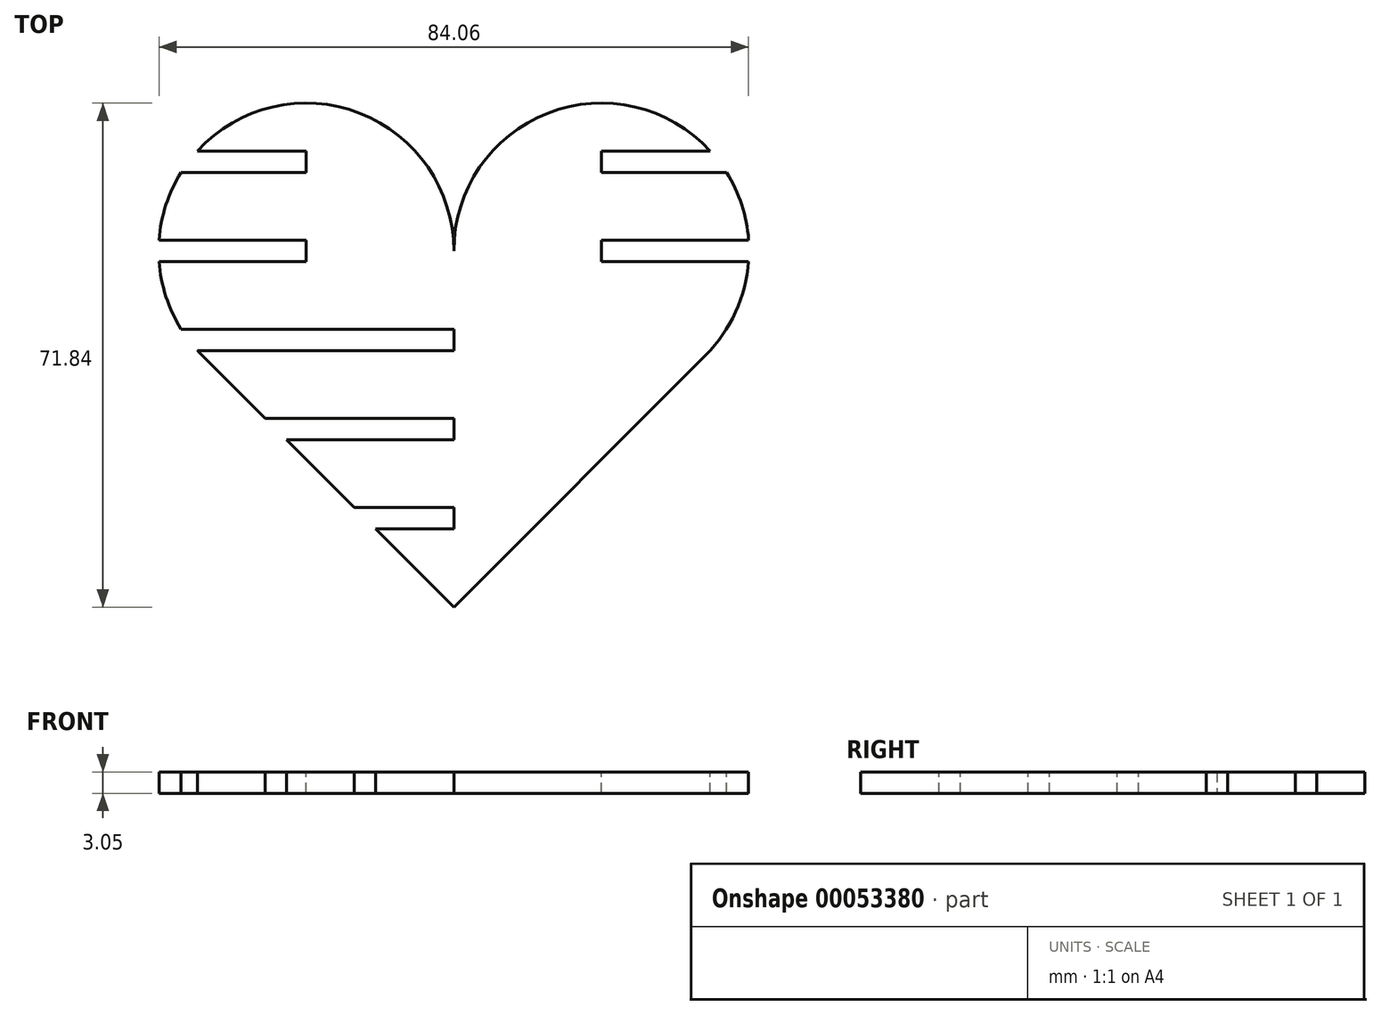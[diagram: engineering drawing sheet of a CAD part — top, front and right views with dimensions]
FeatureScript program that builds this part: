
annotation { "Feature Type Name" : "Feature", "Feature Type Description" : "" }
export const myFeature = defineFeature(function(context is Context, id is Id, definition is map)
    precondition{}
    {
        {
            var Q0;
            Q0=qCreatedBy(makeId("Top.planeOp"),FACE);
            var sketch = newSketch(context, id + "F0", { "sketchPlane" : qUnion([Q0])});
            skLineSegment(sketch, "E0", {"start": v(-50.8, 0) * mm, "end": v(0, -50.8) * mm});
            skLineSegment(sketch, "E1", {"start": v(0, -50.8) * mm, "end": v(50.8, 0) * mm});
            skLineSegment(sketch, "E2", {"start": v(-50.8, 0) * mm, "end": v(50.8, 0) * mm, "construction": true});
            skCircle(sketch, "E3", {"center": v(-21.04, 0) * mm, "radius": 21.04 * mm});
            skCircle(sketch, "E4", {"center": v(21.04, 0) * mm, "radius": 21.04 * mm});
            skSolve(sketch);
        }
        {
            var Q0;
            {var subQ0=sQuery(id+"F0.wireOp",EDGE,"E3");var subQ1=makeQuery(id+"F0.imprint","INTERSECT",VERTEX,{"derivedFrom":[sQuery(id+"F0.wireOp",EDGE,"E0"),subQ0]});Q0=makeQuery(id+"F0.imprint","IMPRINT",FACE,{"disambiguationData":[TD([[makeQuery(id+"F0.imprint","IMPRINT",EDGE,{"disambiguationData":[TD([[subQ1,1.0]])],"derivedFrom":subQ0}),1.0]])]});}
            var Q1;
            {var subQ0=sQuery(id+"F0.wireOp",EDGE,"E4");var subQ1=makeQuery(id+"F0.imprint","INTERSECT",VERTEX,{"derivedFrom":[sQuery(id+"F0.wireOp",EDGE,"E1"),subQ0]});Q1=makeQuery(id+"F0.imprint","IMPRINT",FACE,{"disambiguationData":[TD([[makeQuery(id+"F0.imprint","IMPRINT",EDGE,{"disambiguationData":[TD([[subQ1,1.0]])],"derivedFrom":subQ0}),1.0]])]});}
            var Q2;
            {var subQ0=sQuery(id+"F0.wireOp",EDGE,"E1");var subQ1=sQuery(id+"F0.wireOp",EDGE,"E0");var subQ2=makeQuery(id+"F0.imprint","INTERSECT",VERTEX,{"derivedFrom":[subQ1,subQ0]});Q2=makeQuery(id+"F0.imprint","IMPRINT",FACE,{"disambiguationData":[TD([[makeQuery(id+"F0.imprint","IMPRINT",EDGE,{"disambiguationData":[TD([[subQ2,1.0]])],"derivedFrom":subQ1}),1.0]])]});}
            extrude(context, id + "F1", {"entities" : qUnion([Q0, Q1, Q2]), "depth" : 3.05 * mm});
        }
        {
            var Q0;
            Q0=makeQuery(id+"F1.opExtrude","CAP_FACE",FACE,{"disambiguationData":[OSD([sQuery(id+"F0.wireOp",EDGE,"E0"),sQuery(id+"F0.wireOp",EDGE,"E1"),sQuery(id+"F0.wireOp",EDGE,"E3"),sQuery(id+"F0.wireOp",EDGE,"E4")])],"isStart":false});
            var sketch = newSketch(context, id + "F2", { "sketchPlane" : qUnion([Q0])});
            skCircle(sketch, "E5", {"center": v(-21.04, 0) * mm, "radius": 21.04 * mm, "construction": true});
            skCircle(sketch, "E6", {"center": v(21.04, 0) * mm, "radius": 21.04 * mm, "construction": true});
            skLineSegment(sketch, "E7.bottom", {"start": v(-42.08, -1.52) * mm, "end": v(-21.04, -1.52) * mm});
            skLineSegment(sketch, "E7.top", {"start": v(-42.08, 1.52) * mm, "end": v(-21.04, 1.52) * mm});
            skLineSegment(sketch, "E7.left", {"start": v(-42.08, -1.52) * mm, "end": v(-42.08, 1.52) * mm});
            skLineSegment(sketch, "E7.right", {"start": v(-21.04, -1.52) * mm, "end": v(-21.04, 1.52) * mm});
            skLineSegment(sketch, "E8.bottom", {"start": v(21.04, -1.52) * mm, "end": v(42.08, -1.52) * mm});
            skLineSegment(sketch, "E8.top", {"start": v(21.04, 1.52) * mm, "end": v(42.08, 1.52) * mm});
            skLineSegment(sketch, "E8.left", {"start": v(21.04, -1.52) * mm, "end": v(21.04, 1.52) * mm});
            skLineSegment(sketch, "E8.right", {"start": v(42.08, -1.52) * mm, "end": v(42.08, 1.52) * mm});
            skPoint(sketch, "E9", {"position": v(-42.08, 0) * mm});
            skPoint(sketch, "E10", {"position": v(42.08, 0) * mm});
            skLineSegment(sketch, "E11", {"start": v(0, -50.8) * mm, "end": v(0, -25.4) * mm, "construction": true});
            skLineSegment(sketch, "E12", {"start": v(0, -25.4) * mm, "end": v(0, 0) * mm, "construction": true});
            skPoint(sketch, "E13", {"position": v(0, -12.7) * mm});
            skPoint(sketch, "E14", {"position": v(0, -38.1) * mm});
            skLineSegment(sketch, "E15.bottom", {"start": v(-38.87, -14.22) * mm, "end": v(0, -14.22) * mm});
            skLineSegment(sketch, "E15.top", {"start": v(-38.87, -11.18) * mm, "end": v(0, -11.18) * mm});
            skLineSegment(sketch, "E15.left", {"start": v(-38.87, -14.22) * mm, "end": v(-38.87, -11.18) * mm});
            skLineSegment(sketch, "E15.right", {"start": v(0, -14.22) * mm, "end": v(0, -11.18) * mm});
            skLineSegment(sketch, "E16.bottom", {"start": v(-26.92, -26.92) * mm, "end": v(0, -26.92) * mm});
            skLineSegment(sketch, "E16.top", {"start": v(-26.92, -23.88) * mm, "end": v(0, -23.88) * mm});
            skLineSegment(sketch, "E16.left", {"start": v(-26.92, -26.92) * mm, "end": v(-26.92, -23.88) * mm});
            skLineSegment(sketch, "E16.right", {"start": v(0, -26.92) * mm, "end": v(0, -23.88) * mm});
            skLineSegment(sketch, "E17.bottom", {"start": v(-14.22, -39.62) * mm, "end": v(0, -39.62) * mm});
            skLineSegment(sketch, "E17.top", {"start": v(-14.22, -36.58) * mm, "end": v(0, -36.58) * mm});
            skLineSegment(sketch, "E17.left", {"start": v(-14.22, -39.62) * mm, "end": v(-14.22, -36.58) * mm});
            skLineSegment(sketch, "E17.right", {"start": v(0, -39.62) * mm, "end": v(0, -36.58) * mm});
            skLineSegment(sketch, "E18.bottom", {"start": v(-38.87, 11.18) * mm, "end": v(-21.04, 11.18) * mm});
            skLineSegment(sketch, "E18.top", {"start": v(-38.87, 14.22) * mm, "end": v(-21.04, 14.22) * mm});
            skLineSegment(sketch, "E18.left", {"start": v(-38.87, 14.22) * mm, "end": v(-38.87, 11.18) * mm});
            skLineSegment(sketch, "E18.right", {"start": v(-21.04, 14.22) * mm, "end": v(-21.04, 11.18) * mm});
            skCircle(sketch, "E19", {"center": v(0, 0) * mm, "radius": 12.7 * mm, "construction": true});
            skPoint(sketch, "E20", {"position": v(-38.87, -12.7) * mm});
            skPoint(sketch, "E21", {"position": v(-26.92, -25.4) * mm});
            skPoint(sketch, "E22", {"position": v(-14.22, -38.1) * mm});
            skPoint(sketch, "E23", {"position": v(-38.87, 12.7) * mm});
            skLineSegment(sketch, "E24", {"start": v(-21.04, 12.7) * mm, "end": v(21.04, 12.7) * mm, "construction": true});
            skLineSegment(sketch, "E25.bottom", {"start": v(21.04, 14.22) * mm, "end": v(38.87, 14.22) * mm});
            skLineSegment(sketch, "E25.top", {"start": v(21.04, 11.18) * mm, "end": v(38.87, 11.18) * mm});
            skLineSegment(sketch, "E25.left", {"start": v(21.04, 14.22) * mm, "end": v(21.04, 11.18) * mm});
            skLineSegment(sketch, "E25.right", {"start": v(38.87, 14.22) * mm, "end": v(38.87, 11.18) * mm});
            skPoint(sketch, "E26", {"position": v(38.87, 12.7) * mm});
            skSolve(sketch);
        }
        {
            var Q0;
            {var subQ0=sQuery(id+"F2.wireOp",EDGE,"E18.bottom");Q0=makeQuery(id+"F2.imprint","IMPRINT",FACE,{"disambiguationData":[TD([[makeQuery(id+"F2.imprint","IMPRINT",EDGE,{"derivedFrom":subQ0}),1.0]])]});}
            var Q1;
            {var subQ4=sQuery(id+"F2.wireOp",EDGE,"E25.top");Q1=makeQuery(id+"F2.imprint","IMPRINT",FACE,{"disambiguationData":[TD([[makeQuery(id+"F2.imprint","IMPRINT",EDGE,{"derivedFrom":subQ4}),1.0]])]});}
            var Q2;
            {var subQ0=sQuery(id+"F2.wireOp",EDGE,"E8.left");Q2=makeQuery(id+"F2.imprint","IMPRINT",FACE,{"disambiguationData":[TD([[makeQuery(id+"F2.imprint","IMPRINT",EDGE,{"derivedFrom":subQ0}),-1.0]])]});}
            var Q3;
            {var subQ4=sQuery(id+"F2.wireOp",EDGE,"E7.right");Q3=makeQuery(id+"F2.imprint","IMPRINT",FACE,{"disambiguationData":[TD([[makeQuery(id+"F2.imprint","IMPRINT",EDGE,{"derivedFrom":subQ4}),1.0]])]});}
            var Q4;
            {var subQ0=sQuery(id+"F2.wireOp",EDGE,"E15.right");Q4=makeQuery(id+"F2.imprint","IMPRINT",FACE,{"disambiguationData":[TD([[makeQuery(id+"F2.imprint","IMPRINT",EDGE,{"derivedFrom":subQ0}),1.0]])]});}
            var Q5;
            {var subQ4=sQuery(id+"F2.wireOp",EDGE,"E16.top");Q5=makeQuery(id+"F2.imprint","IMPRINT",FACE,{"disambiguationData":[TD([[makeQuery(id+"F2.imprint","IMPRINT",EDGE,{"derivedFrom":subQ4}),-1.0]])]});}
            var Q6;
            {var subQ4=sQuery(id+"F2.wireOp",EDGE,"E17.top");Q6=makeQuery(id+"F2.imprint","IMPRINT",FACE,{"disambiguationData":[TD([[makeQuery(id+"F2.imprint","IMPRINT",EDGE,{"derivedFrom":subQ4}),-1.0]])]});}
            extrude(context, id + "F3", {"entities" : qUnion([Q0, Q1, Q2, Q3, Q4, Q5, Q6]), "operationType" : NewBodyOperationType.REMOVE, "endBound" : BoundingType.THROUGH_ALL, "oppositeDirection" : true, "depth" : 25.4 * mm});
        }
    });
